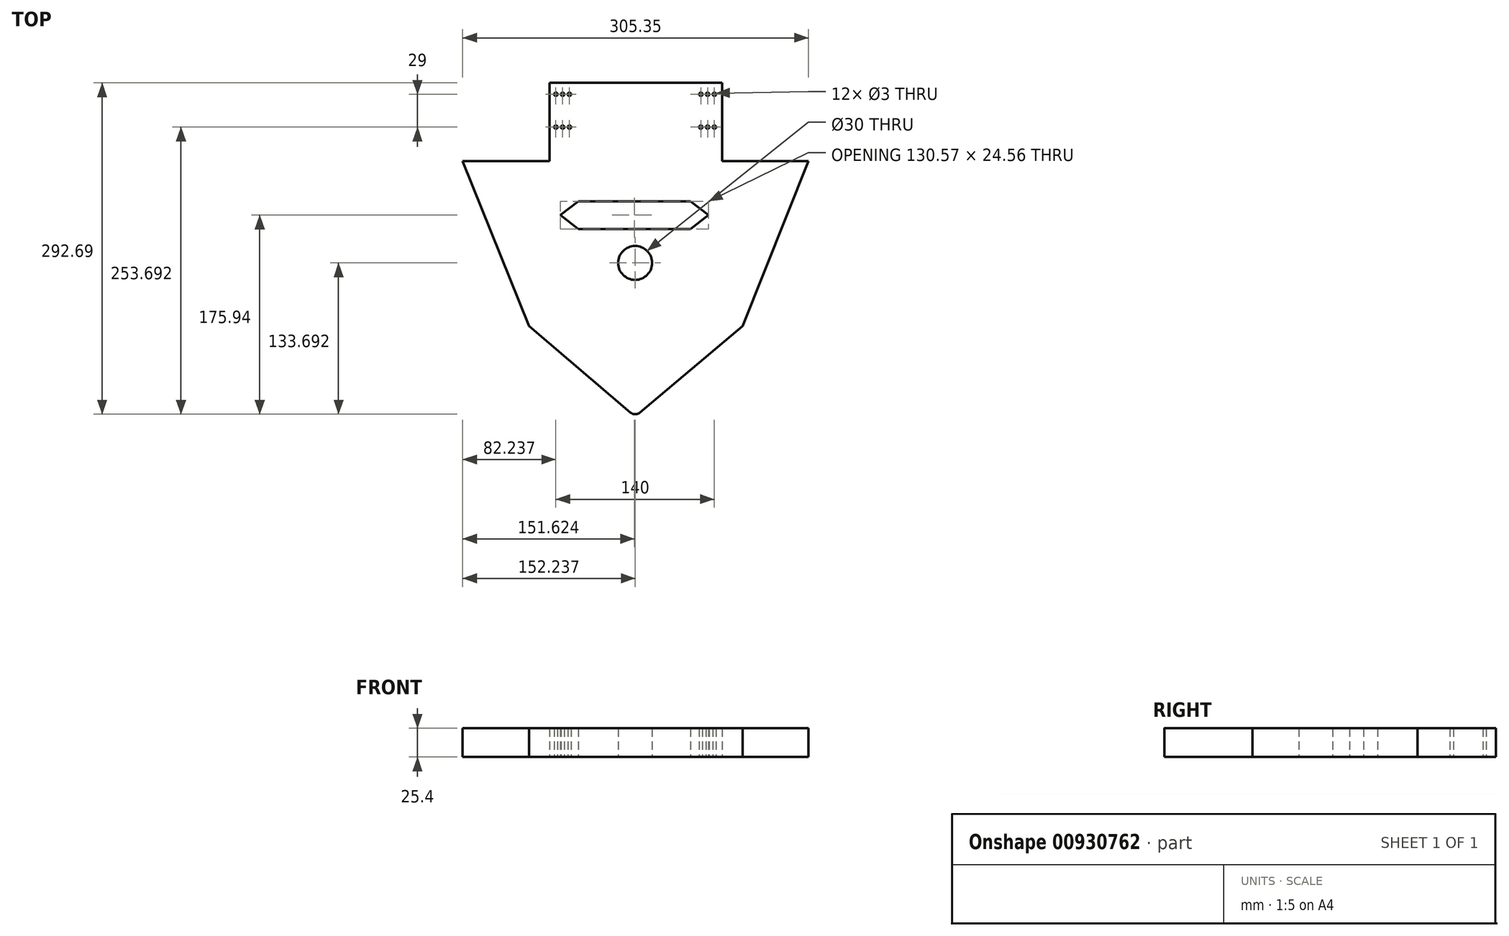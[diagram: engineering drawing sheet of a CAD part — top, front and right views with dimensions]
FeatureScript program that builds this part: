
annotation { "Feature Type Name" : "Feature", "Feature Type Description" : "" }
export const myFeature = defineFeature(function(context is Context, id is Id, definition is map)
    precondition{}
    {
        {
            var Q0;
            Q0=qCreatedBy(makeId("Top.planeOp"),FACE);
            var sketch = newSketch(context, id + "F0", { "sketchPlane" : qUnion([Q0])});
            skCircle(sketch, "E0", {"center": v(-69.36, 63.91) * mm, "radius": 1.5 * mm});
            skCircle(sketch, "E1.0.1.0", {"center": v(-69.36, 92.91) * mm, "radius": 1.5 * mm});
            skCircle(sketch, "E1.1.0.0", {"center": v(-63.36, 63.91) * mm, "radius": 1.5 * mm});
            skCircle(sketch, "E1.1.1.0", {"center": v(-63.36, 92.91) * mm, "radius": 1.5 * mm});
            skCircle(sketch, "E1.2.0.0", {"center": v(-57.36, 63.91) * mm, "radius": 1.5 * mm});
            skCircle(sketch, "E1.2.1.0", {"center": v(-57.36, 92.91) * mm, "radius": 1.5 * mm});
            skLineSegment(sketch, "E1.direction1", {"start": v(-69.36, 63.91) * mm, "end": v(-63.36, 63.91) * mm, "construction": true});
            skLineSegment(sketch, "E1.direction2", {"start": v(-69.36, 63.91) * mm, "end": v(-69.36, 92.91) * mm, "construction": true});
            skLineSegment(sketch, "E2", {"start": v(0.64, 66.92) * mm, "end": v(0.64, 94.72) * mm});
            skCircle(sketch, "E3.MirrorC", {"center": v(70.64, 92.91) * mm, "radius": 1.5 * mm});
            skLineSegment(sketch, "E4.MirrorCS", {"start": v(70.64, 63.91) * mm, "end": v(64.64, 63.91) * mm, "construction": true});
            skCircle(sketch, "E5.MirrorC", {"center": v(58.64, 63.91) * mm, "radius": 1.5 * mm});
            skCircle(sketch, "E6.MirrorC", {"center": v(70.64, 63.91) * mm, "radius": 1.5 * mm});
            skCircle(sketch, "E7.MirrorC", {"center": v(64.64, 63.91) * mm, "radius": 1.5 * mm});
            skCircle(sketch, "E8.MirrorC", {"center": v(64.64, 92.91) * mm, "radius": 1.5 * mm});
            skCircle(sketch, "E9.MirrorC", {"center": v(58.64, 92.91) * mm, "radius": 1.5 * mm});
            skLineSegment(sketch, "E10.MirrorCS", {"start": v(70.64, 63.91) * mm, "end": v(70.64, 92.91) * mm, "construction": true});
            skLineSegment(sketch, "E11.bottom", {"start": v(-74.9, 102.91) * mm, "end": v(77.4, 102.91) * mm});
            skLineSegment(sketch, "E11.left", {"start": v(-74.9, 102.91) * mm, "end": v(-74.9, -100.04) * mm});
            skLineSegment(sketch, "E11.right", {"start": v(77.4, 102.91) * mm, "end": v(77.4, -100.04) * mm});
            skPoint(sketch, "E12", {"position": v(-68.82, 102.91) * mm});
            skCircle(sketch, "E13", {"center": v(0.64, -56.09) * mm, "radius": 15 * mm});
            skLineSegment(sketch, "E14", {"start": v(-74.9, 33.91) * mm, "end": v(-93.16, 25.76) * mm});
            skLineSegment(sketch, "E15", {"start": v(77.4, 33.91) * mm, "end": v(95.66, 25.76) * mm});
            skLineSegment(sketch, "E16", {"start": v(-65.26, -13.84) * mm, "end": v(-49.48, -1.56) * mm});
            skLineSegment(sketch, "E17", {"start": v(-49.48, -1.56) * mm, "end": v(49.52, -1.56) * mm});
            skLineSegment(sketch, "E18", {"start": v(49.52, -1.56) * mm, "end": v(65.31, -13.84) * mm});
            skLineSegment(sketch, "E19", {"start": v(65.31, -13.84) * mm, "end": v(49.52, -26.12) * mm});
            skLineSegment(sketch, "E20", {"start": v(49.52, -26.12) * mm, "end": v(-49.48, -26.12) * mm});
            skLineSegment(sketch, "E21", {"start": v(-49.48, -26.12) * mm, "end": v(-65.26, -13.84) * mm});
            skLineSegment(sketch, "E22", {"start": v(-49.48, -1.56) * mm, "end": v(-49.48, -26.12) * mm});
            skLineSegment(sketch, "E23", {"start": v(49.52, -1.56) * mm, "end": v(49.52, -26.12) * mm});
            skCircle(sketch, "E24", {"center": v(-61.26, -13.84) * mm, "radius": 1.6 * mm});
            skCircle(sketch, "E25", {"center": v(61.31, -13.84) * mm, "radius": 1.6 * mm});
            skLineSegment(sketch, "E26", {"start": v(0.64, -56.09) * mm, "end": v(48.18, -56.09) * mm});
            skLineSegment(sketch, "E27", {"start": v(-74.9, -111.98) * mm, "end": v(-74.9, -100.04) * mm});
            skPoint(sketch, "E28.end.orphan", {"position": v(77.4, -114.37) * mm});
            skLineSegment(sketch, "E29", {"start": v(-93.16, 25.76) * mm, "end": v(-93.16, -111.98) * mm});
            skLineSegment(sketch, "E30", {"start": v(95.66, 25.76) * mm, "end": v(95.66, -111.98) * mm});
            skLineSegment(sketch, "E31", {"start": v(95.66, -111.98) * mm, "end": v(4.75, -188.3) * mm});
            skLineSegment(sketch, "E32", {"start": v(-3.45, -188.27) * mm, "end": v(-93.16, -111.98) * mm});
            skPoint(sketch, "E33.visualSharp", {"position": v(0.64, -191.75) * mm});
            skArc(sketch, "E33.filletArc", {"start": v(-3.45, -188.27) * mm, "mid": v(0.64, -189.78) * mm, "end": v(4.75, -188.3) * mm});
            skPoint(sketch, "E34.end.orphan", {"position": v(-151.6, 25.76) * mm});
            skPoint(sketch, "E35.end.orphan", {"position": v(144.83, 25.76) * mm});
            skLineSegment(sketch, "E36", {"start": v(-74.9, 33.91) * mm, "end": v(-151.6, 33.91) * mm});
            skLineSegment(sketch, "E37", {"start": v(77.4, 33.91) * mm, "end": v(153.75, 33.91) * mm});
            skLineSegment(sketch, "E38", {"start": v(-151.6, 33.91) * mm, "end": v(-93.16, -111.98) * mm});
            skLineSegment(sketch, "E39", {"start": v(95.66, -111.98) * mm, "end": v(153.75, 33.91) * mm});
            skSolve(sketch);
        }
        {
            var Q0;
            Q0 = qSketchRegion(id + "F0", true);
            extrude(context, id + "F1", {"entities" : qUnion([Q0]), "depth" : 25.4 * mm, "offsetDistance" : 25.4 * mm});
        }
    });
